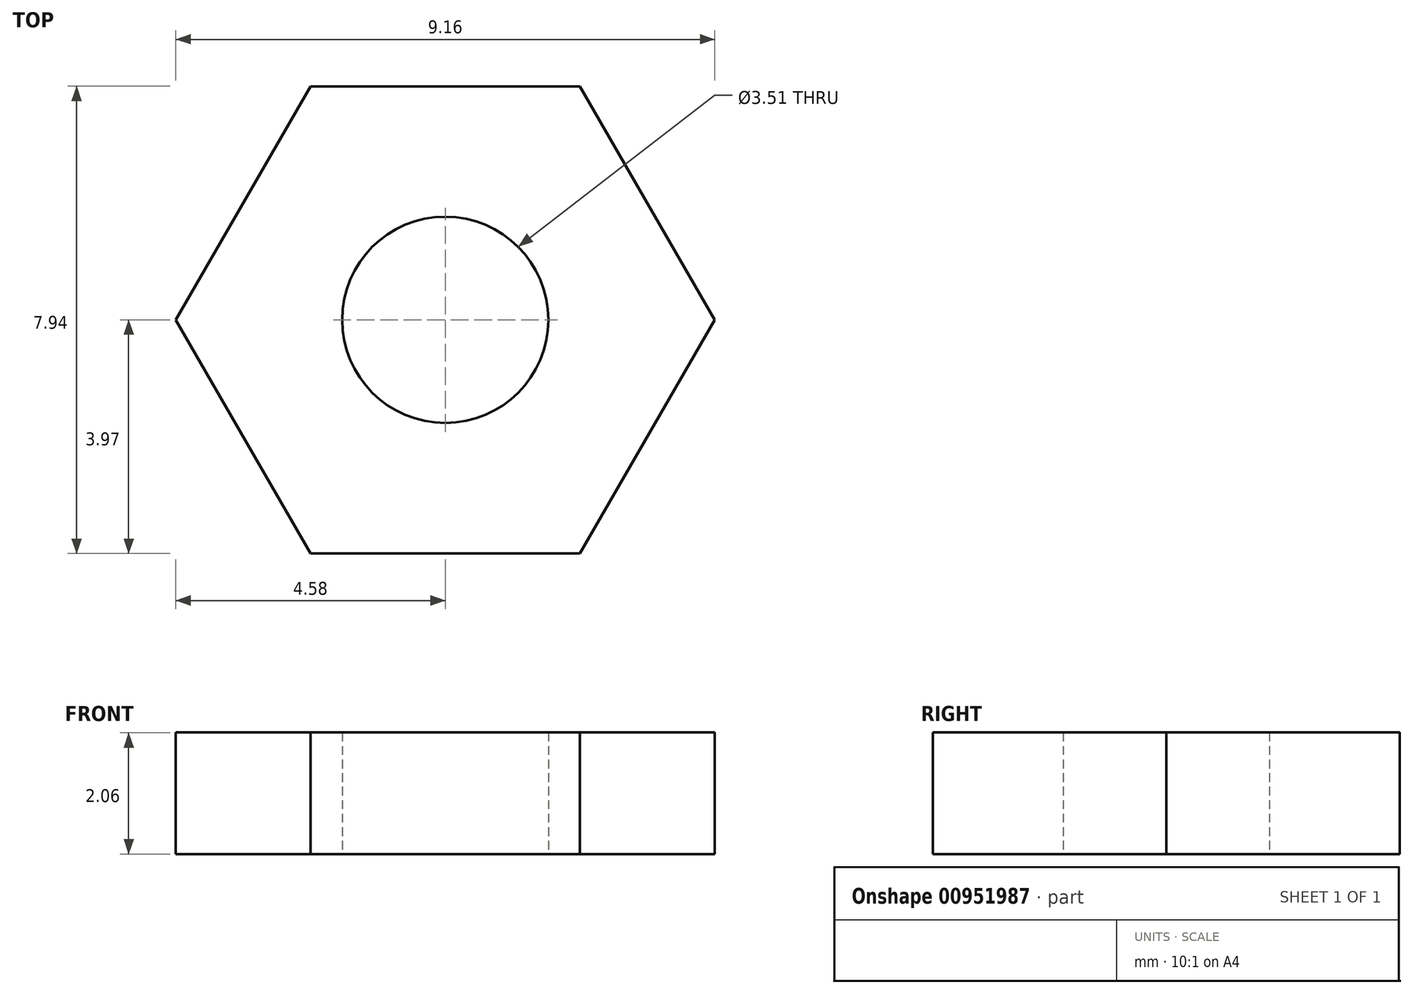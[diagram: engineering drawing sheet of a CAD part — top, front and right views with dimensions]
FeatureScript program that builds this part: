
annotation { "Feature Type Name" : "Feature", "Feature Type Description" : "" }
export const myFeature = defineFeature(function(context is Context, id is Id, definition is map)
    precondition{}
    {
        {
            var Q0;
            Q0=qCreatedBy(makeId("Top.planeOp"),FACE);
            var sketch = newSketch(context, id + "F0", { "sketchPlane" : qUnion([Q0])});
            skCircle(sketch, "E0.cCircle", {"center": v(0, 0) * mm, "radius": 3.97 * mm, "construction": true});
            skLineSegment(sketch, "E0.0", {"start": v(-2.3, 3.97) * mm, "end": v(2.3, 3.97) * mm});
            skLineSegment(sketch, "E0.1", {"start": v(2.3, 3.97) * mm, "end": v(4.58, 0) * mm});
            skLineSegment(sketch, "E0.2", {"start": v(4.58, 0) * mm, "end": v(2.3, -3.97) * mm});
            skLineSegment(sketch, "E0.3", {"start": v(2.3, -3.97) * mm, "end": v(-2.3, -3.97) * mm});
            skLineSegment(sketch, "E0.4", {"start": v(-2.3, -3.97) * mm, "end": v(-4.58, 0) * mm});
            skLineSegment(sketch, "E0.5", {"start": v(-4.58, 0) * mm, "end": v(-2.3, 3.97) * mm});
            skPoint(sketch, "E0.0.midPoint", {"position": v(0, 3.97) * mm});
            skCircle(sketch, "E1", {"center": v(0, 0) * mm, "radius": 1.75 * mm});
            skSolve(sketch);
        }
        {
            var Q0;
            Q0=makeQuery(id+"F0.imprint","IMPRINT",FACE,{"disambiguationData":[TD([[makeQuery(id+"F0.imprint","IMPRINT",EDGE,{"derivedFrom":sQuery(id+"F0.wireOp",EDGE,"E0.0")}),-1.0]])]});
            extrude(context, id + "F1", {"entities" : qUnion([Q0]), "endBound" : BoundingType.SYMMETRIC, "depth" : 2.07 * mm, "offsetDistance" : 25.4 * mm});
        }
        {
            var Q0;
            Q0=makeQuery(id+"F1.opExtrude","CAP_FACE",FACE,{"disambiguationData":[OSD([sQuery(id+"F0.wireOp",EDGE,"E0.0"),sQuery(id+"F0.wireOp",EDGE,"E0.1"),sQuery(id+"F0.wireOp",EDGE,"E0.2"),sQuery(id+"F0.wireOp",EDGE,"E0.3"),sQuery(id+"F0.wireOp",EDGE,"E0.4"),sQuery(id+"F0.wireOp",EDGE,"E0.5"),sQuery(id+"F0.wireOp",EDGE,"E1")])],"isStart":false});
            cPlane(context, id + "F2", {"entities" : qUnion([Q0]), "cplaneType" : CPlaneType.OFFSET, "offset" : ((0.1 - 0.08) / 2) * mm, "width" : 152.4 * mm, "height" : 152.4 * mm});
        }
    });
